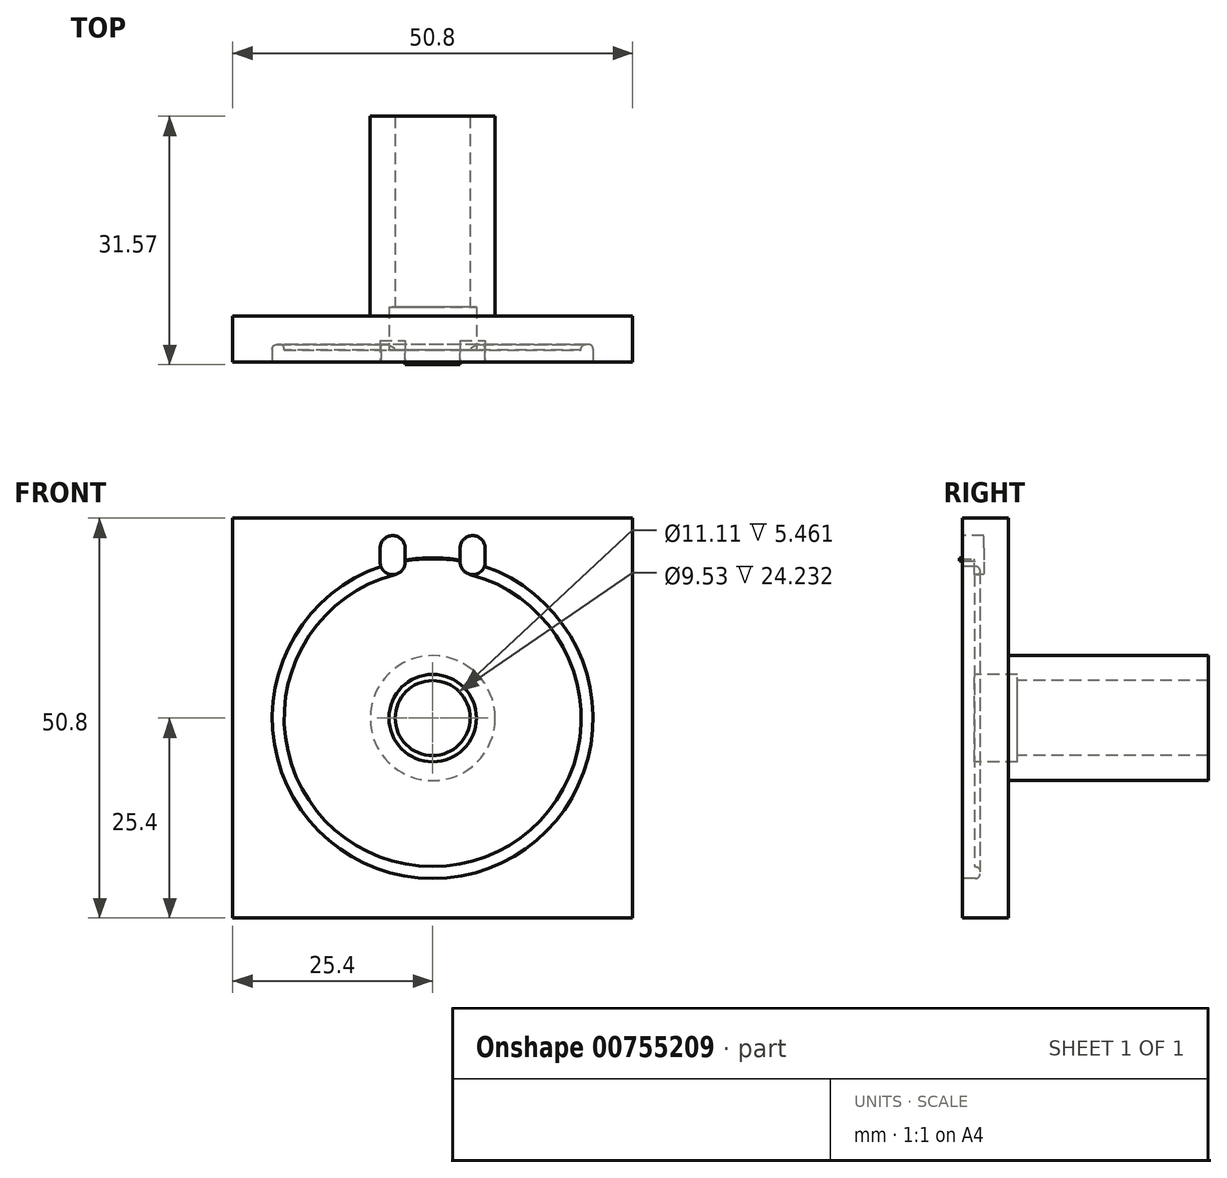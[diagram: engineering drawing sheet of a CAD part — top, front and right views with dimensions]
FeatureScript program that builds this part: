
annotation { "Feature Type Name" : "Feature", "Feature Type Description" : "" }
export const myFeature = defineFeature(function(context is Context, id is Id, definition is map)
    precondition{}
    {
        {
            var Q0;
            Q0=qCreatedBy(makeId("Front.planeOp"),FACE);
            var sketch = newSketch(context, id + "F0", { "sketchPlane" : qUnion([Q0])});
            skLineSegment(sketch, "E0.bottom", {"start": v(-25.4, 25.4) * mm, "end": v(25.4, 25.4) * mm});
            skLineSegment(sketch, "E0.top", {"start": v(-25.4, -25.4) * mm, "end": v(25.4, -25.4) * mm});
            skLineSegment(sketch, "E0.left", {"start": v(-25.4, 25.4) * mm, "end": v(-25.4, -25.4) * mm});
            skLineSegment(sketch, "E0.right", {"start": v(25.4, 25.4) * mm, "end": v(25.4, -25.4) * mm});
            skCircle(sketch, "E1.converted", {"center": v(0, 0) * mm, "radius": 20.37 * mm});
            skSolve(sketch);
        }
        {
            var Q0;
            Q0 = qSketchRegion(id + "F0", true);
            extrude(context, id + "F1", {"entities" : qUnion([Q0]), "oppositeDirection" : true, "depth" : 5.84 * mm, "offsetDistance" : 25.4 * mm});
        }
        {
            var Q0;
            Q0=qCreatedBy(makeId("Right.planeOp"),FACE);
            var sketch = newSketch(context, id + "F2", { "sketchPlane" : qUnion([Q0])});
            skLineSegment(sketch, "E2", {"start": v(31.24, 4.76) * mm, "end": v(7.01, 4.76) * mm});
            skLineSegment(sketch, "E3", {"start": v(1.55, 5.56) * mm, "end": v(1.55, 20.37) * mm});
            skLineSegment(sketch, "E4", {"start": v(1.55, 20.37) * mm, "end": v(5.84, 20.37) * mm});
            skLineSegment(sketch, "E5", {"start": v(5.84, 20.37) * mm, "end": v(5.84, 7.94) * mm});
            skLineSegment(sketch, "E6", {"start": v(5.84, 7.94) * mm, "end": v(31.24, 7.94) * mm});
            skLineSegment(sketch, "E7", {"start": v(31.24, 7.94) * mm, "end": v(31.24, 4.76) * mm});
            skLineSegment(sketch, "E8", {"start": v(0, 0) * mm, "end": v(13.54, 0) * mm, "construction": true});
            skLineSegment(sketch, "E9.bottom", {"start": v(1.55, 5.56) * mm, "end": v(7.01, 5.56) * mm});
            skLineSegment(sketch, "E9.right", {"start": v(7.01, 5.56) * mm, "end": v(7.01, 4.76) * mm});
            skSolve(sketch);
        }
        {
            var Q0;
            Q0 = qSketchRegion(id + "F2", true);
            var Q1;
            Q1=sQuery(id+"F2.wireOp",EDGE,"E8");
            revolve(context, id + "F3", {"operationType" : NewBodyOperationType.ADD, "surfaceOperationType" : NewSurfaceOperationType.NEW, "entities" : qUnion([Q0]), "axis" : qUnion([Q1]), "revolveType" : RevolveType.FULL});
        }
        {
            var Q0;
            Q0=qCreatedBy(makeId("Right.planeOp"),FACE);
            var sketch = newSketch(context, id + "F4", { "sketchPlane" : qUnion([Q0])});
            skLineSegment(sketch, "E10", {"start": v(0, 0) * mm, "end": v(-15.68, 0) * mm, "construction": true});
            skSolve(sketch);
        }
        {
            var Q0;
            Q0=sQuery(id+"F4.wireOp",EDGE,"E10");
            cPlane(context, id + "F5", {"entities" : qUnion([Q0]), "cplaneType" : CPlaneType.LINE_ANGLE, "offset" : 25.4 * mm, "angle" : 75 * degree, "oppositeDirection" : true, "width" : 152.4 * mm, "height" : 152.4 * mm});
        }
        {
            var Q0;
            Q0=qCreatedBy(id+"F5.planeOp",FACE);
            var sketch = newSketch(context, id + "F6", { "sketchPlane" : qUnion([Q0])});
            skLineSegment(sketch, "E11", {"start": v(-1.66, 19.77) * mm, "end": v(-1.66, 19.46) * mm, "construction": true});
            skArc(sketch, "E12", {"start": v(-1.66, 20.37) * mm, "mid": v(-2.09, 20.2) * mm, "end": v(-2.26, 19.77) * mm});
            skLineSegment(sketch, "E13", {"start": v(-2.26, 19.77) * mm, "end": v(-2.26, 19.46) * mm});
            skLineSegment(sketch, "E14", {"start": v(-1.55, 20.37) * mm, "end": v(-1.55, 18.86) * mm});
            skLineSegment(sketch, "E15", {"start": v(-1.55, 20.37) * mm, "end": v(-1.66, 20.37) * mm});
            skArc(sketch, "E16", {"start": v(-2.26, 19.46) * mm, "mid": v(-2.09, 19.03) * mm, "end": v(-1.66, 18.86) * mm});
            skLineSegment(sketch, "E17", {"start": v(-1.66, 18.86) * mm, "end": v(-1.55, 18.86) * mm});
            skSolve(sketch);
        }
        {
            var Q0;
            Q0 = qSketchRegion(id + "F6", true);
            var Q1;
            Q1=sQuery(id+"F4.wireOp",EDGE,"E10");
            revolve(context, id + "F7", {"operationType" : NewBodyOperationType.REMOVE, "surfaceOperationType" : NewSurfaceOperationType.NEW, "entities" : qUnion([Q0]), "axis" : qUnion([Q1]), "revolveType" : RevolveType.ONE_DIRECTION, "angle" : 330 * degree});
        }
        {
            var Q0;
            Q0=makeQuery(id+"F1.opExtrude","CAP_FACE",FACE,{"disambiguationData":[OSD([sQuery(id+"F0.wireOp",EDGE,"E0.bottom"),sQuery(id+"F0.wireOp",EDGE,"E0.top"),sQuery(id+"F0.wireOp",EDGE,"E0.left"),sQuery(id+"F0.wireOp",EDGE,"E0.right"),sQuery(id+"F0.wireOp",EDGE,"E1.converted")])],"isStart":true});
            var sketch = newSketch(context, id + "F8", { "sketchPlane" : qUnion([Q0])});
            skLineSegment(sketch, "E18.bottom", {"start": v(-5.08, 21.59) * mm, "end": v(5.08, 21.59) * mm, "construction": true});
            skLineSegment(sketch, "E18.top", {"start": v(-5.08, 19.81) * mm, "end": v(5.08, 19.81) * mm, "construction": true});
            skLineSegment(sketch, "E18.left", {"start": v(-5.08, 21.59) * mm, "end": v(-5.08, 19.81) * mm, "construction": true});
            skLineSegment(sketch, "E18.right", {"start": v(5.08, 21.59) * mm, "end": v(5.08, 19.81) * mm, "construction": true});
            skArc(sketch, "E19", {"start": v(-3.5, 21.59) * mm, "mid": v(-5.08, 23.18) * mm, "end": v(-6.67, 21.59) * mm});
            skArc(sketch, "E20", {"start": v(-6.67, 19.81) * mm, "mid": v(-5.08, 18.22) * mm, "end": v(-3.5, 19.81) * mm});
            skArc(sketch, "E21", {"start": v(3.5, 19.81) * mm, "mid": v(5.08, 18.22) * mm, "end": v(6.67, 19.81) * mm});
            skArc(sketch, "E22", {"start": v(6.67, 21.59) * mm, "mid": v(5.08, 23.18) * mm, "end": v(3.5, 21.59) * mm});
            skLineSegment(sketch, "E23", {"start": v(-6.67, 21.59) * mm, "end": v(-6.67, 19.81) * mm});
            skLineSegment(sketch, "E24", {"start": v(-3.5, 21.59) * mm, "end": v(-3.5, 19.81) * mm});
            skLineSegment(sketch, "E25", {"start": v(3.5, 21.59) * mm, "end": v(3.5, 19.81) * mm});
            skLineSegment(sketch, "E26", {"start": v(6.67, 21.59) * mm, "end": v(6.67, 19.81) * mm});
            skSolve(sketch);
        }
        {
            var Q0;
            Q0 = qSketchRegion(id + "F8", true);
            extrude(context, id + "F9", {"entities" : qUnion([Q0]), "operationType" : NewBodyOperationType.REMOVE, "oppositeDirection" : true, "depth" : 2.74 * mm, "offsetDistance" : 25.4 * mm});
        }
        {
            var Q0;
            Q0=makeQuery(id+"F3.opRevolve","SWEPT_FACE",FACE,{"disambiguationData":[OSD([sQuery(id+"F2.wireOp",EDGE,"E3")])]});
            var sketch = newSketch(context, id + "F10", { "sketchPlane" : qUnion([Q0])});
            skArc(sketch, "E27.0", {"start": v(3.5, 20.07) * mm, "mid": v(0, 20.37) * mm, "end": v(-3.5, 20.07) * mm});
            skLineSegment(sketch, "E28.0", {"start": v(-3.5, 19.94) * mm, "end": v(-3.5, 20.07) * mm});
            skLineSegment(sketch, "E29.0", {"start": v(3.5, 19.94) * mm, "end": v(3.5, 20.07) * mm});
            skArc(sketch, "E30", {"start": v(3.5, 19.94) * mm, "mid": v(0, 20.24) * mm, "end": v(-3.5, 19.94) * mm});
            skPoint(sketch, "E31.orphan", {"position": v(-3.5, 19.81) * mm});
            skPoint(sketch, "E32.orphan", {"position": v(3.5, 19.81) * mm});
            skSolve(sketch);
        }
        {
            var Q0;
            Q0 = qSketchRegion(id + "F10", true);
            extrude(context, id + "F11", {"entities" : qUnion([Q0]), "operationType" : NewBodyOperationType.ADD, "depth" : 1.88 * mm, "offsetDistance" : 25.4 * mm});
        }
    });
